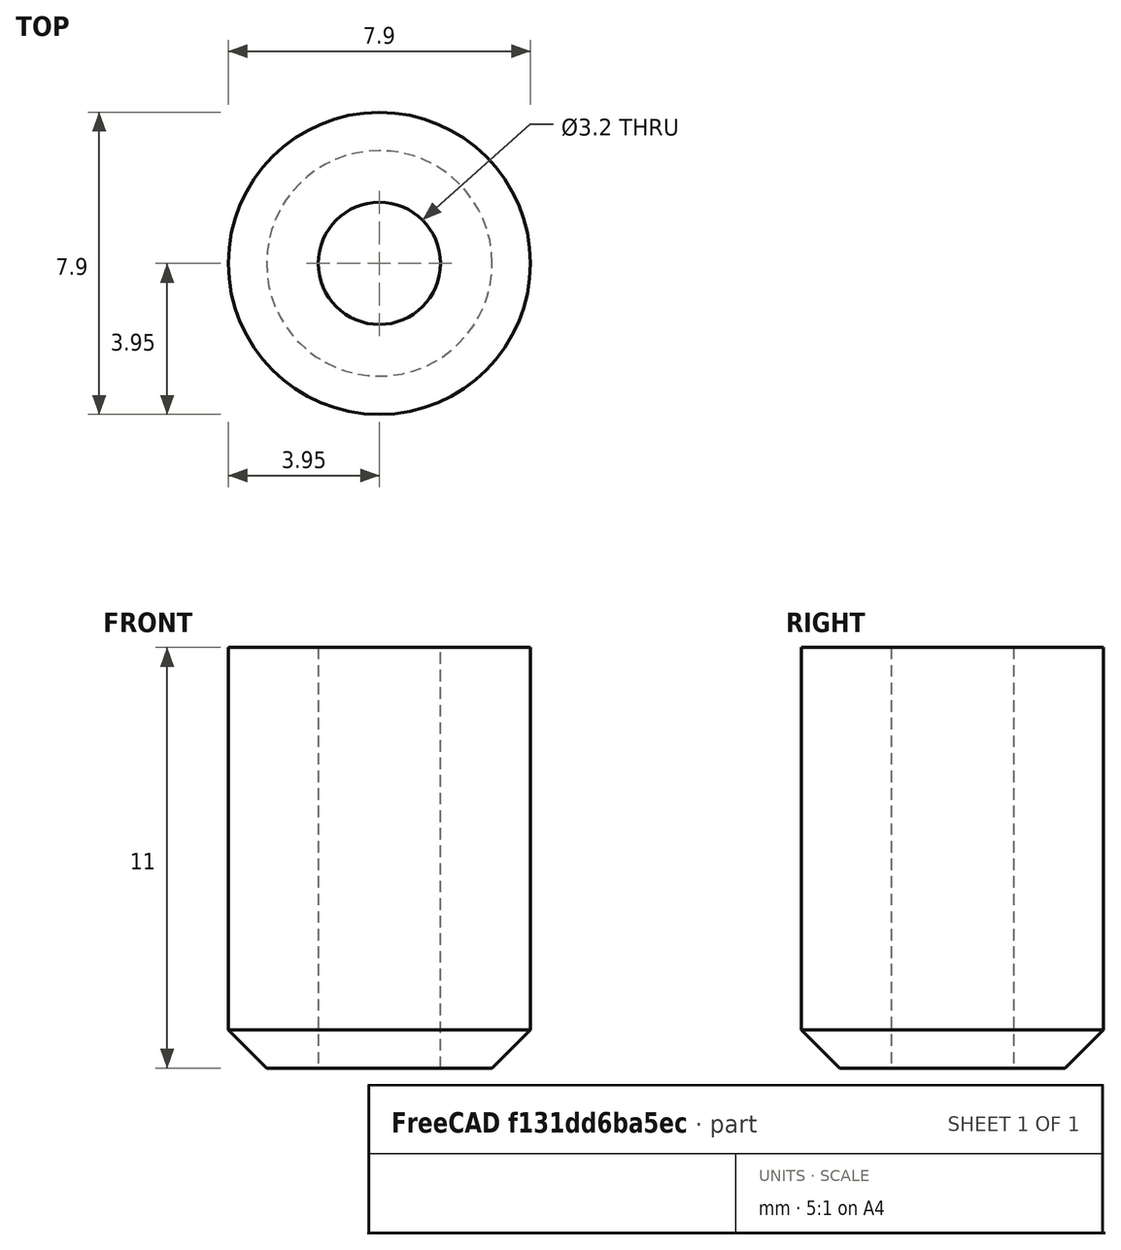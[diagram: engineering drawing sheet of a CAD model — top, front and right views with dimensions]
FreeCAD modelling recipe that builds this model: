
FCSTD DOCUMENT  (FreeCAD 0.20R29603 (Git))
Label: 7900-3200-11000
License: All rights reserved
LicenseURL: http://en.wikipedia.org/wiki/All_rights_reserved
objects: Sketcher::SketchObject×1, PartDesign::Pad×1, PartDesign::Chamfer×1, PartDesign::Body×1
note: 6 computed .brp shape members not serialized (recipe doc carries the construction recipe); baked Part::Feature solids carry a one-line shape summary decoded from their .brp

FEATURE [Sketcher::SketchObject] Sketch
  FullyConstrained = true
  MapMode = 5
  Support = -> [XY_Plane]
  sketch-geometry (4):
    g0: Circle CenterX=0 CenterY=0 CenterZ=0 NormalX=0 NormalY=0 NormalZ=1 AngleXU=0 Radius=3.95
    g1: Circle CenterX=0 CenterY=0 CenterZ=0 NormalX=0 NormalY=0 NormalZ=1 AngleXU=0 Radius=1.6
    g2: GeomPoint X=3.95 Y=0 Z=0
    g3: GeomPoint X=1.6 Y=0 Z=0
  constraints (8):
    c: Coincident(g0,g-1)
    c: Coincident(g1,g0)
    c: Radius(g1) = 1.6
    c: PointOnObject(g3,g1)
    c: PointOnObject(g3,g-1)
    c: PointOnObject(g2,g0)
    c: PointOnObject(g2,g-1)
    c: Diameter(g0) = 7.9
FEATURE [PartDesign::Pad] Pad
  Direction = (0,0,1)
  Length = 11
  Length2 = 10
  Profile = -> Sketch
  ReferenceAxis = -> Sketch [N_Axis]
  Type = 0
FEATURE [PartDesign::Chamfer] Chamfer
  Angle = 45
  Base = -> Pad [Edge2]
  BaseFeature = -> Pad
  ChamferType = 0
  FlipDirection = false
  Size = 1
  Size2 = 1
  SupportTransform = false
  UseAllEdges = false
FEATURE [PartDesign::Body] Body
  Group = -> [Sketch,Pad,Chamfer]
  Origin = -> Origin
  Tip = -> Chamfer
